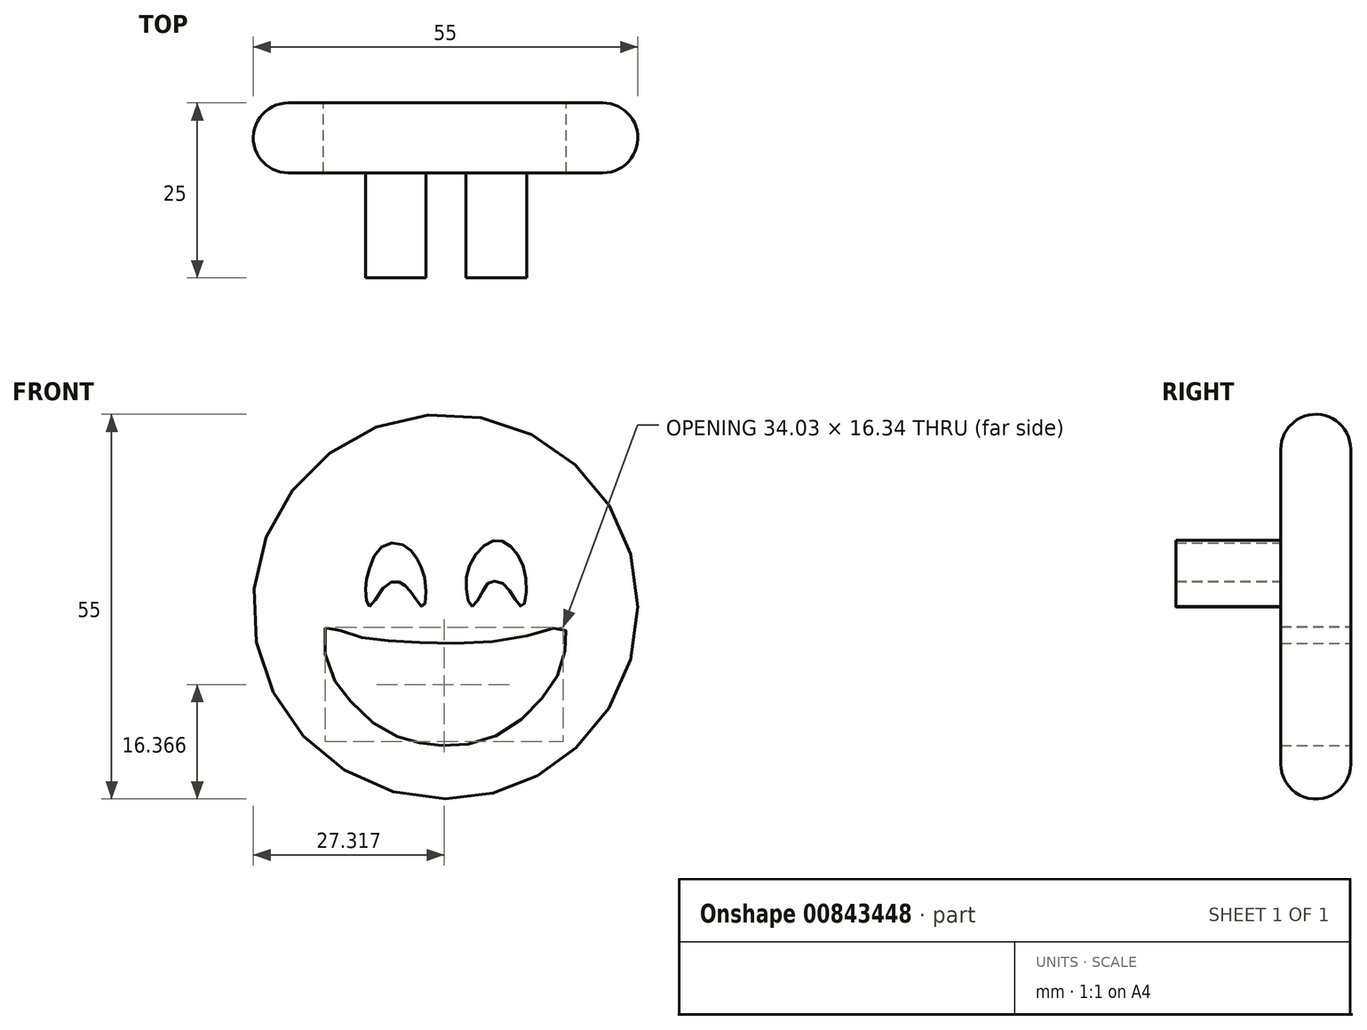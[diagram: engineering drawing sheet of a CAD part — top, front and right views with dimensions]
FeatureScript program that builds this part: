
annotation { "Feature Type Name" : "Feature", "Feature Type Description" : "" }
export const myFeature = defineFeature(function(context is Context, id is Id, definition is map)
    precondition{}
    {
        {
            var Q0;
            Q0=qCreatedBy(makeId("Front.planeOp"),FACE);
            var sketch = newSketch(context, id + "F0", { "sketchPlane" : qUnion([Q0])});
            skCircle(sketch, "E0", {"center": v(0, 0) * mm, "radius": 27.5 * mm});
            skSolve(sketch);
        }
        {
            var Q0;
            Q0 = qSketchRegion(id + "F0", true);
            extrude(context, id + "F1", {"entities" : qUnion([Q0]), "endBound" : BoundingType.SYMMETRIC, "depth" : 10 * mm, "offsetDistance" : 25 * mm});
        }
        {
            var Q0;
            Q0=makeQuery(id+"F1.opExtrude","CAP_FACE",FACE,{"disambiguationData":[OSD([sQuery(id+"F0.wireOp",EDGE,"E0")])],"isStart":false});
            var sketch = newSketch(context, id + "F2", { "sketchPlane" : qUnion([Q0])});
            skFitSpline(sketch, "E1", {"points": [v(-10.87, 0) * mm, v(-11.43, 1.97) * mm, v(-11, 5.05) * mm, v(-8.95, 8.71) * mm, v(-5.79, 8.71) * mm, v(-4.03, 6.7) * mm, v(-2.93, 3.65) * mm, v(-3.18, 0) * mm, v(-4.29, 1.1) * mm, v(-5.59, 2.85) * mm, v(-6.64, 3.5) * mm, v(-8.65, 3) * mm, v(-10.87, 0) * mm]});
            skSolve(sketch);
        }
        {
            var Q0;
            Q0=makeQuery(id+"F2.imprint","IMPRINT",FACE,{"disambiguationData":[TD([[makeQuery(id+"F2.imprint","IMPRINT",EDGE,{"derivedFrom":sQuery(id+"F2.wireOp",EDGE,"E1")}),1.0]])]});
            var sketch = newSketch(context, id + "F3", { "sketchPlane" : qUnion([Q0])});
            skFitSpline(sketch, "E2", {"points": [v(3.79, 0) * mm, v(5.3, 2.2) * mm, v(6.37, 3.51) * mm, v(8.17, 3.32) * mm, v(9.92, 1.08) * mm, v(10.95, 0) * mm, v(11.58, 2.73) * mm, v(10.56, 7.07) * mm, v(8.32, 9.26) * mm, v(6.03, 9.07) * mm, v(3.4, 5.85) * mm, v(3, 2.15) * mm, v(3.79, 0) * mm]});
            skSolve(sketch);
        }
        {
            var Q0;
            Q0=makeQuery(id+"F2.imprint","IMPRINT",FACE,{"disambiguationData":[TD([[makeQuery(id+"F2.imprint","IMPRINT",EDGE,{"derivedFrom":sQuery(id+"F2.wireOp",EDGE,"E1")}),1.0]])]});
            var sketch = newSketch(context, id + "F4", { "sketchPlane" : qUnion([Q0])});
            skFitSpline(sketch, "E3", {"points": [v(-17.2, -3.02) * mm, v(-15.88, -3.07) * mm, v(-12.76, -4.24) * mm, v(-7.85, -4.87) * mm, v(0, -5.24) * mm, v(9.78, -4.55) * mm, v(15.54, -3.07) * mm, v(17.02, -3.07) * mm, v(17.23, -4.87) * mm, v(16.28, -9.3) * mm, v(13.27, -13.69) * mm, v(8.41, -17.86) * mm, v(2.55, -19.76) * mm, v(-2, -19.7) * mm, v(-5.16, -19.13) * mm, v(-9.75, -17.12) * mm, v(-14.5, -12.42) * mm, v(-16.73, -8.67) * mm, v(-17.2, -3.02) * mm]});
            skSolve(sketch);
        }
        {
            var Q0;
            Q0=makeQuery(id+"F2.imprint","IMPRINT",FACE,{"disambiguationData":[TD([[makeQuery(id+"F2.imprint","IMPRINT",EDGE,{"derivedFrom":sQuery(id+"F2.wireOp",EDGE,"E1")}),-1.0]])]});
            extrude(context, id + "F5", {"entities" : qUnion([Q0]), "operationType" : NewBodyOperationType.ADD, "depth" : 15 * mm, "offsetDistance" : 25 * mm});
        }
        {
            var Q0;
            Q0=makeQuery(id+"F3.imprint","IMPRINT",FACE,{"disambiguationData":[TD([[makeQuery(id+"F3.imprint","IMPRINT",EDGE,{"derivedFrom":sQuery(id+"F3.wireOp",EDGE,"E2")}),1.0]])]});
            extrude(context, id + "F6", {"entities" : qUnion([Q0]), "operationType" : NewBodyOperationType.ADD, "depth" : 15 * mm, "offsetDistance" : 25 * mm});
        }
        {
            var Q0;
            Q0=makeQuery(id+"F4.imprint","IMPRINT",FACE,{"disambiguationData":[TD([[makeQuery(id+"F4.imprint","IMPRINT",EDGE,{"derivedFrom":sQuery(id+"F4.wireOp",EDGE,"E3")}),-1.0]])]});
            extrude(context, id + "F7", {"entities" : qUnion([Q0]), "operationType" : NewBodyOperationType.REMOVE, "endBound" : BoundingType.THROUGH_ALL, "oppositeDirection" : true, "depth" : 25 * mm, "offsetDistance" : 25 * mm});
        }
        {
            var Q0;
            Q0=makeQuery(id+"F1.opExtrude","SWEPT_FACE",FACE,{"disambiguationData":[OSD([sQuery(id+"F0.wireOp",EDGE,"E0")])]});
            fillet(context, id + "F8", {"entities" : qUnion([Q0]), "radius" : 5 * mm, "tangentPropagation" : true, "allowEdgeOverflow" : false});
        }
    });
